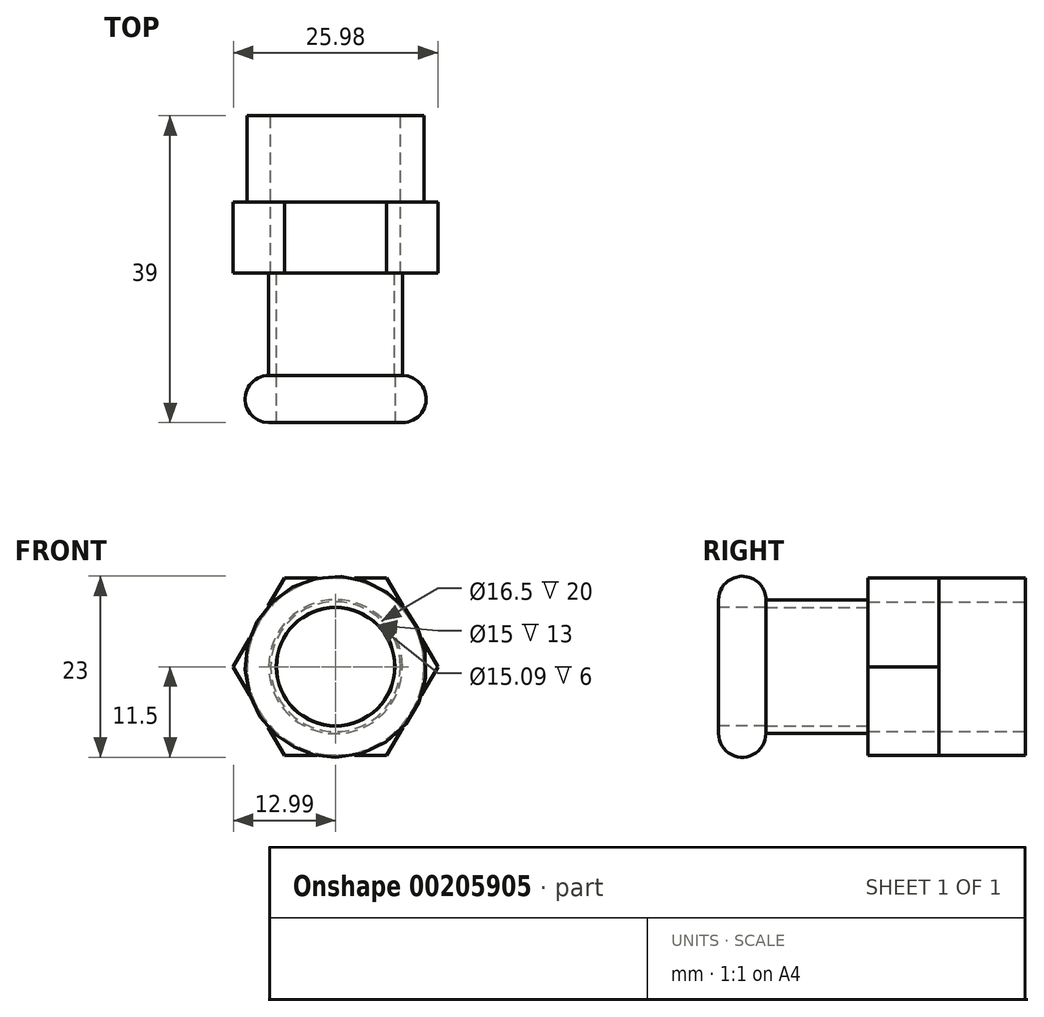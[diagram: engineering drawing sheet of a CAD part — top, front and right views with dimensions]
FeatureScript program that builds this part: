
annotation { "Feature Type Name" : "Feature", "Feature Type Description" : "" }
export const myFeature = defineFeature(function(context is Context, id is Id, definition is map)
    precondition{}
    {
        {
            var Q0;
            Q0=qCreatedBy(makeId("Front.planeOp"),FACE);
            var sketch = newSketch(context, id + "F0", { "sketchPlane" : qUnion([Q0])});
            skCircle(sketch, "E0", {"center": v(0, 0) * mm, "radius": 8.25 * mm});
            skCircle(sketch, "E1", {"center": v(0, 0) * mm, "radius": 11.25 * mm});
            skSolve(sketch);
        }
        {
            var Q0;
            Q0=makeQuery(id+"F0.imprint","IMPRINT",FACE,{"disambiguationData":[TD([[makeQuery(id+"F0.imprint","IMPRINT",EDGE,{"derivedFrom":sQuery(id+"F0.wireOp",EDGE,"E0")}),-1.0]])]});
            extrude(context, id + "F1", {"entities" : qUnion([Q0]), "depth" : 11 * mm});
        }
        {
            var Q0;
            Q0=makeQuery(id+"F1.opExtrude","CAP_FACE",FACE,{"disambiguationData":[OSD([sQuery(id+"F0.wireOp",EDGE,"E0"),sQuery(id+"F0.wireOp",EDGE,"E1")])],"isStart":false});
            var sketch = newSketch(context, id + "F2", { "sketchPlane" : qUnion([Q0])});
            skCircle(sketch, "E2.cCircle", {"center": v(0, 0) * mm, "radius": 11.25 * mm, "construction": true});
            skLineSegment(sketch, "E2.0", {"start": v(-6.5, 11.25) * mm, "end": v(6.5, 11.25) * mm});
            skLineSegment(sketch, "E2.1", {"start": v(6.5, 11.25) * mm, "end": v(13, 0) * mm});
            skLineSegment(sketch, "E2.2", {"start": v(13, 0) * mm, "end": v(6.5, -11.25) * mm});
            skLineSegment(sketch, "E2.3", {"start": v(6.5, -11.25) * mm, "end": v(-6.5, -11.25) * mm});
            skLineSegment(sketch, "E2.4", {"start": v(-6.5, -11.25) * mm, "end": v(-13, 0) * mm});
            skLineSegment(sketch, "E2.5", {"start": v(-13, 0) * mm, "end": v(-6.5, 11.25) * mm});
            skPoint(sketch, "E2.0.midPoint", {"position": v(0, 11.25) * mm});
            skCircle(sketch, "E3", {"center": v(0, 0) * mm, "radius": 8.25 * mm});
            skSolve(sketch);
        }
        {
            var Q0;
            Q0 = qSketchRegion(id + "F2", true);
            extrude(context, id + "F3", {"entities" : qUnion([Q0]), "operationType" : NewBodyOperationType.ADD, "depth" : 9 * mm});
        }
        {
            var Q0;
            Q0=makeQuery(id+"F3.opExtrude","CAP_FACE",FACE,{"disambiguationData":[OSD([sQuery(id+"F2.wireOp",EDGE,"E2.0"),sQuery(id+"F2.wireOp",EDGE,"E2.1"),sQuery(id+"F2.wireOp",EDGE,"E2.2"),sQuery(id+"F2.wireOp",EDGE,"E2.3"),sQuery(id+"F2.wireOp",EDGE,"E2.4"),sQuery(id+"F2.wireOp",EDGE,"E2.5"),sQuery(id+"F2.wireOp",EDGE,"E3")])],"isStart":false});
            var sketch = newSketch(context, id + "F4", { "sketchPlane" : qUnion([Q0])});
            skCircle(sketch, "E4", {"center": v(0, 0) * mm, "radius": 8.5 * mm});
            skCircle(sketch, "E5", {"center": v(0, 0) * mm, "radius": 7.5 * mm});
            skSolve(sketch);
        }
        {
            var Q0;
            Q0 = qSketchRegion(id + "F4", true);
            extrude(context, id + "F5", {"entities" : qUnion([Q0]), "operationType" : NewBodyOperationType.ADD, "depth" : 13 * mm});
        }
        {
            var Q0;
            Q0=qCreatedBy(makeId("Top.planeOp"),FACE);
            var sketch = newSketch(context, id + "F6", { "sketchPlane" : qUnion([Q0])});
            skArc(sketch, "E6", {"start": v(8.5, -39) * mm, "mid": v(11.5, -36) * mm, "end": v(8.5, -33) * mm});
            skLineSegment(sketch, "E7", {"start": v(8.5, -33) * mm, "end": v(8.5, -39) * mm, "construction": true});
            skLineSegment(sketch, "E8", {"start": v(8.5, -33) * mm, "end": v(7.54, -33) * mm});
            skLineSegment(sketch, "E9", {"start": v(7.54, -33) * mm, "end": v(7.54, -39) * mm});
            skLineSegment(sketch, "E10", {"start": v(7.54, -39) * mm, "end": v(8.5, -39) * mm});
            skLineSegment(sketch, "E11", {"start": v(0, -40.52) * mm, "end": v(0, -30.14) * mm, "construction": true});
            skSolve(sketch);
        }
        {
            var Q0;
            Q0=makeQuery(id+"F6.imprint","IMPRINT",FACE,{"disambiguationData":[TD([[makeQuery(id+"F6.imprint","IMPRINT",EDGE,{"derivedFrom":sQuery(id+"F6.wireOp",EDGE,"E6")}),1.0]])]});
            var Q1;
            Q1=sQuery(id+"F6.wireOp",EDGE,"E11");
            revolve(context, id + "F7", {"operationType" : NewBodyOperationType.ADD, "entities" : qUnion([Q0]), "axis" : qUnion([Q1]), "revolveType" : RevolveType.FULL});
        }
    });
